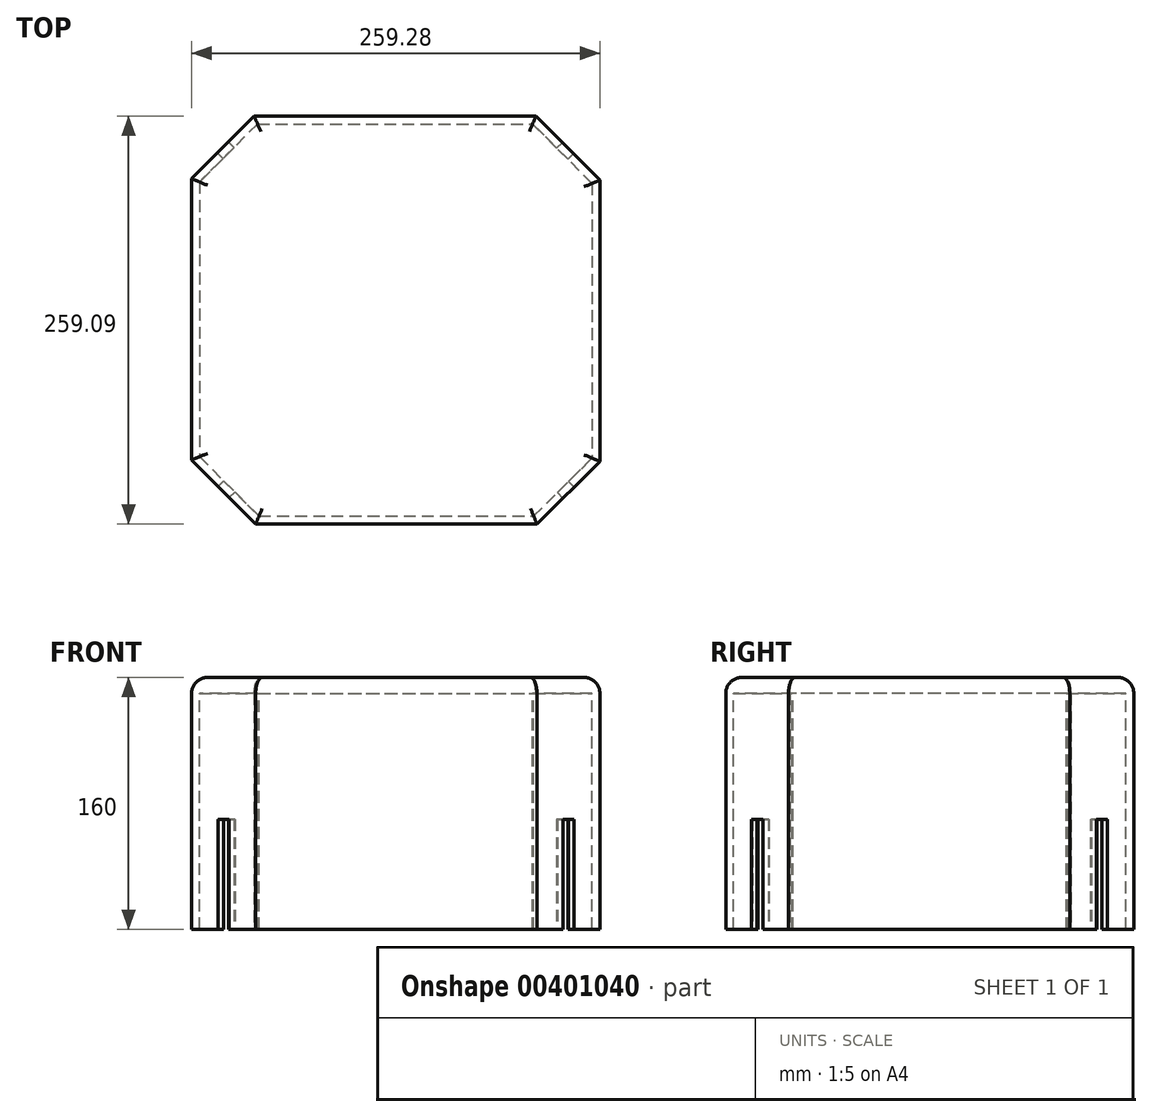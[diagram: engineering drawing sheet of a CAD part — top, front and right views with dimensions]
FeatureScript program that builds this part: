
annotation { "Feature Type Name" : "Feature", "Feature Type Description" : "" }
export const myFeature = defineFeature(function(context is Context, id is Id, definition is map)
    precondition{}
    {
        {
            var Q0;
            Q0=qCreatedBy(makeId("Top.planeOp"),FACE);
            var sketch = newSketch(context, id + "F0", { "sketchPlane" : qUnion([Q0])});
            skLineSegment(sketch, "E0.bottom", {"start": v(-147.8, 75.06) * mm, "end": v(26.87, 75.06) * mm});
            skLineSegment(sketch, "E0.top", {"start": v(-146.9, -174.03) * mm, "end": v(27.58, -174.03) * mm});
            skLineSegment(sketch, "E0.left", {"start": v(-184.66, 38.2) * mm, "end": v(-184.66, -136.28) * mm});
            skLineSegment(sketch, "E0.right", {"start": v(64.62, 37.3) * mm, "end": v(64.62, -137.18) * mm});
            skLineSegment(sketch, "E1", {"start": v(-184.66, -136.28) * mm, "end": v(-146.9, -174.03) * mm});
            skLineSegment(sketch, "E2", {"start": v(27.58, -174.03) * mm, "end": v(64.62, -137.18) * mm});
            skLineSegment(sketch, "E3", {"start": v(64.62, 37.3) * mm, "end": v(26.87, 75.06) * mm});
            skLineSegment(sketch, "E4", {"start": v(-147.8, 75.06) * mm, "end": v(-184.66, 38.2) * mm});
            skLineSegment(sketch, "E5.0", {"start": v(-149.87, 80.06) * mm, "end": v(28.94, 80.06) * mm});
            skLineSegment(sketch, "E5.1", {"start": v(69.62, 39.38) * mm, "end": v(28.94, 80.06) * mm});
            skLineSegment(sketch, "E5.2", {"start": v(-149.87, 80.06) * mm, "end": v(-189.66, 40.28) * mm});
            skLineSegment(sketch, "E5.3", {"start": v(69.62, 39.38) * mm, "end": v(69.62, -139.25) * mm});
            skLineSegment(sketch, "E5.4", {"start": v(-189.66, 40.28) * mm, "end": v(-189.66, -138.35) * mm});
            skLineSegment(sketch, "E5.5", {"start": v(-189.66, -138.35) * mm, "end": v(-148.97, -179.03) * mm});
            skLineSegment(sketch, "E5.6", {"start": v(-148.97, -179.03) * mm, "end": v(29.64, -179.03) * mm});
            skLineSegment(sketch, "E5.7", {"start": v(29.64, -179.03) * mm, "end": v(69.62, -139.25) * mm});
            skSolve(sketch);
        }
        {
            var Q0;
            Q0=makeQuery(id+"F0.imprint","IMPRINT",FACE,{"disambiguationData":[TD([[makeQuery(id+"F0.imprint","IMPRINT",EDGE,{"derivedFrom":sQuery(id+"F0.wireOp",EDGE,"E0.bottom")}),-1.0]])]});
            var Q1;
            Q1=makeQuery(id+"F0.imprint","IMPRINT",FACE,{"disambiguationData":[TD([[makeQuery(id+"F0.imprint","IMPRINT",EDGE,{"derivedFrom":sQuery(id+"F0.wireOp",EDGE,"E0.bottom")}),1.0]])]});
            extrude(context, id + "F1", {"entities" : qUnion([Q0, Q1]), "depth" : 10 * mm});
        }
        {
            var Q0;
            Q0=makeQuery(id+"F0.imprint","IMPRINT",FACE,{"disambiguationData":[TD([[makeQuery(id+"F0.imprint","IMPRINT",EDGE,{"derivedFrom":sQuery(id+"F0.wireOp",EDGE,"E0.bottom")}),1.0]])]});
            extrude(context, id + "F2", {"entities" : qUnion([Q0]), "operationType" : NewBodyOperationType.ADD, "oppositeDirection" : true, "depth" : 150 * mm});
        }
        {
            var Q0;
            {var subQ0=sQuery(id+"F0.wireOp",EDGE,"E5.5");Q0=makeQuery(id+"F2.boolean.opBoolean","MERGE",FACE,{"derivedFrom":[makeQuery(id+"F1.opExtrude","SWEPT_FACE",FACE,{"disambiguationData":[OSD([subQ0])]}),makeQuery(id+"F2.opExtrude","SWEPT_FACE",FACE,{"disambiguationData":[OSD([subQ0])]})]});}
            var sketch = newSketch(context, id + "F3", { "sketchPlane" : qUnion([Q0])});
            skPoint(sketch, "E6.centerSnap0", {"position": v(-7.51, -150) * mm});
            skLineSegment(sketch, "E7.bottom", {"start": v(-12.51, -80) * mm, "end": v(-2.51, -80) * mm});
            skLineSegment(sketch, "E7.top", {"start": v(-12.51, -150) * mm, "end": v(-2.51, -150) * mm});
            skLineSegment(sketch, "E7.left", {"start": v(-12.51, -80) * mm, "end": v(-12.51, -150) * mm});
            skLineSegment(sketch, "E7.right", {"start": v(-2.51, -80) * mm, "end": v(-2.51, -150) * mm});
            skSolve(sketch);
        }
        {
            var Q0;
            Q0=makeQuery(id+"F3.imprint","IMPRINT",FACE,{"disambiguationData":[TD([[makeQuery(id+"F3.imprint","IMPRINT",EDGE,{"derivedFrom":sQuery(id+"F3.wireOp",EDGE,"E7.bottom")}),-1.0]])]});
            extrude(context, id + "F4", {"entities" : qUnion([Q0]), "operationType" : NewBodyOperationType.REMOVE, "oppositeDirection" : true, "depth" : 25 * mm});
        }
        {
            var Q0;
            Q0=makeQuery(id+"F1.opExtrude","CAP_FACE",FACE,{"disambiguationData":[OSD([sQuery(id+"F0.wireOp",EDGE,"E5.0"),sQuery(id+"F0.wireOp",EDGE,"E5.1"),sQuery(id+"F0.wireOp",EDGE,"E5.2"),sQuery(id+"F0.wireOp",EDGE,"E5.3"),sQuery(id+"F0.wireOp",EDGE,"E5.4"),sQuery(id+"F0.wireOp",EDGE,"E5.5"),sQuery(id+"F0.wireOp",EDGE,"E5.6"),sQuery(id+"F0.wireOp",EDGE,"E5.7")])],"isStart":false});
            fillet(context, id + "F5", {"entities" : qUnion([Q0]), "radius" : 10 * mm, "tangentPropagation" : true, "allowEdgeOverflow" : false});
        }
        {
            var Q0;
            {var subQ0=sQuery(id+"F0.wireOp",EDGE,"E5.7");Q0=makeQuery(id+"F2.boolean.opBoolean","MERGE",FACE,{"derivedFrom":[makeQuery(id+"F1.opExtrude","SWEPT_FACE",FACE,{"disambiguationData":[OSD([subQ0])]}),makeQuery(id+"F2.opExtrude","SWEPT_FACE",FACE,{"disambiguationData":[OSD([subQ0])]})]});}
            var sketch = newSketch(context, id + "F6", { "sketchPlane" : qUnion([Q0])});
            skLineSegment(sketch, "E8.bottom", {"start": v(-82.06, -80) * mm, "end": v(-72.06, -80) * mm});
            skLineSegment(sketch, "E8.top", {"start": v(-82.06, -150) * mm, "end": v(-72.06, -150) * mm});
            skLineSegment(sketch, "E8.left", {"start": v(-82.06, -80) * mm, "end": v(-82.06, -150) * mm});
            skLineSegment(sketch, "E8.right", {"start": v(-72.06, -80) * mm, "end": v(-72.06, -150) * mm});
            skSolve(sketch);
        }
        {
            var Q0;
            {var subQ0=sQuery(id+"F0.wireOp",EDGE,"E5.1");Q0=makeQuery(id+"F2.boolean.opBoolean","MERGE",FACE,{"derivedFrom":[makeQuery(id+"F1.opExtrude","SWEPT_FACE",FACE,{"disambiguationData":[OSD([subQ0])]}),makeQuery(id+"F2.opExtrude","SWEPT_FACE",FACE,{"disambiguationData":[OSD([subQ0])]})]});}
            var sketch = newSketch(context, id + "F7", { "sketchPlane" : qUnion([Q0])});
            skLineSegment(sketch, "E9.bottom", {"start": v(2.38, -80) * mm, "end": v(12.38, -80) * mm});
            skLineSegment(sketch, "E9.top", {"start": v(2.38, -150) * mm, "end": v(12.38, -150) * mm});
            skLineSegment(sketch, "E9.left", {"start": v(2.38, -80) * mm, "end": v(2.38, -150) * mm});
            skLineSegment(sketch, "E9.right", {"start": v(12.38, -80) * mm, "end": v(12.38, -150) * mm});
            skSolve(sketch);
        }
        {
            var Q0;
            {var subQ0=sQuery(id+"F0.wireOp",EDGE,"E5.2");Q0=makeQuery(id+"F2.boolean.opBoolean","MERGE",FACE,{"derivedFrom":[makeQuery(id+"F1.opExtrude","SWEPT_FACE",FACE,{"disambiguationData":[OSD([subQ0])]}),makeQuery(id+"F2.opExtrude","SWEPT_FACE",FACE,{"disambiguationData":[OSD([subQ0])]})]});}
            var sketch = newSketch(context, id + "F8", { "sketchPlane" : qUnion([Q0])});
            skLineSegment(sketch, "E10.bottom", {"start": v(72.5, -80) * mm, "end": v(82.5, -80) * mm});
            skLineSegment(sketch, "E10.top", {"start": v(72.5, -150) * mm, "end": v(82.5, -150) * mm});
            skLineSegment(sketch, "E10.left", {"start": v(72.5, -80) * mm, "end": v(72.5, -150) * mm});
            skLineSegment(sketch, "E10.right", {"start": v(82.5, -80) * mm, "end": v(82.5, -150) * mm});
            skSolve(sketch);
        }
        {
            var Q0;
            Q0=makeQuery(id+"F8.imprint","IMPRINT",FACE,{"disambiguationData":[TD([[makeQuery(id+"F8.imprint","IMPRINT",EDGE,{"derivedFrom":sQuery(id+"F8.wireOp",EDGE,"E10.bottom")}),-1.0]])]});
            extrude(context, id + "F9", {"entities" : qUnion([Q0]), "operationType" : NewBodyOperationType.REMOVE, "oppositeDirection" : true, "depth" : 25 * mm});
        }
        {
            var Q0;
            Q0=makeQuery(id+"F7.imprint","IMPRINT",FACE,{"disambiguationData":[TD([[makeQuery(id+"F7.imprint","IMPRINT",EDGE,{"derivedFrom":sQuery(id+"F7.wireOp",EDGE,"E9.bottom")}),-1.0]])]});
            extrude(context, id + "F10", {"entities" : qUnion([Q0]), "operationType" : NewBodyOperationType.REMOVE, "oppositeDirection" : true, "depth" : 25 * mm});
        }
        {
            var Q0;
            Q0=makeQuery(id+"F6.imprint","IMPRINT",FACE,{"disambiguationData":[TD([[makeQuery(id+"F6.imprint","IMPRINT",EDGE,{"derivedFrom":sQuery(id+"F6.wireOp",EDGE,"E8.bottom")}),-1.0]])]});
            extrude(context, id + "F11", {"entities" : qUnion([Q0]), "operationType" : NewBodyOperationType.REMOVE, "oppositeDirection" : true, "depth" : 25 * mm});
        }
    });
